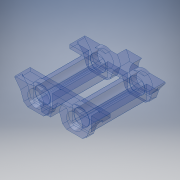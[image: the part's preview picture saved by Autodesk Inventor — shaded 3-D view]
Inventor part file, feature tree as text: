
AUTODESK INVENTOR PART (.ipt)
format: ipt  version: 2019 (Build 230136000, 136)  size: 399,872 bytes
history: native  units: mm
features: mirror x10, extrude x9, sketch x9, chamfer x2, other x1
ambient origin geometry x8: Origin, YZ Plane, XZ Plane, XY Plane, X Axis, Y Axis, Z Axis, Center Point
bodies: Body1 (feature_tree)
feature tree (31):
  other  "Bryła1"
  extrude  "Wyciągnięcie proste1"  Depth=20.0mm
  extrude  "Wyciągnięcie proste2"  Depth=20.0mm
  mirror  "Odbij1"
  extrude  "Wyciągnięcie proste3"  Depth=40.5mm
  mirror  "Odbij2"
  extrude  "Wyciągnięcie proste4"  TaperAngle=0.0deg  [1 undecoded]
  extrude  "Wyciągnięcie proste5"  Depth=40.5mm
  mirror  "Odbij3"
  mirror  "Odbij4"
  extrude  "Wyciągnięcie proste6"  TaperAngle=0.0deg  [1 undecoded]
  mirror  "Odbij5"
  mirror  "Odbij6"
  extrude  "Wyciągnięcie proste7"  Depth=56.02mm
  mirror  "Odbij7"
  chamfer  "Faza1"  Distance=28.01mm
  extrude  "Wyciągnięcie proste8"  Depth=3.6mm TaperAngle=0.0deg
  chamfer  "Faza2"  Distance=7.29mm
  mirror  "Odbij8"
  mirror  "Odbij9"
  extrude  "Wyciągnięcie proste9"  Depth=1.575mm
  mirror  "Odbij10"
  sketch  "Szkic1"
  sketch  "Szkic2"
  sketch  "Szkic3"
  sketch  "Szkic4"
  sketch  "Szkic5"
  sketch  "Szkic6"
  sketch  "Szkic7"
  sketch  "Szkic8"
  sketch  "Szkic10"
note: 2 required parameter values undecoded (feature->parameter linkage not recoverable at this tier; creation-order binding heuristic only, values carry confidence <= 0.55)
